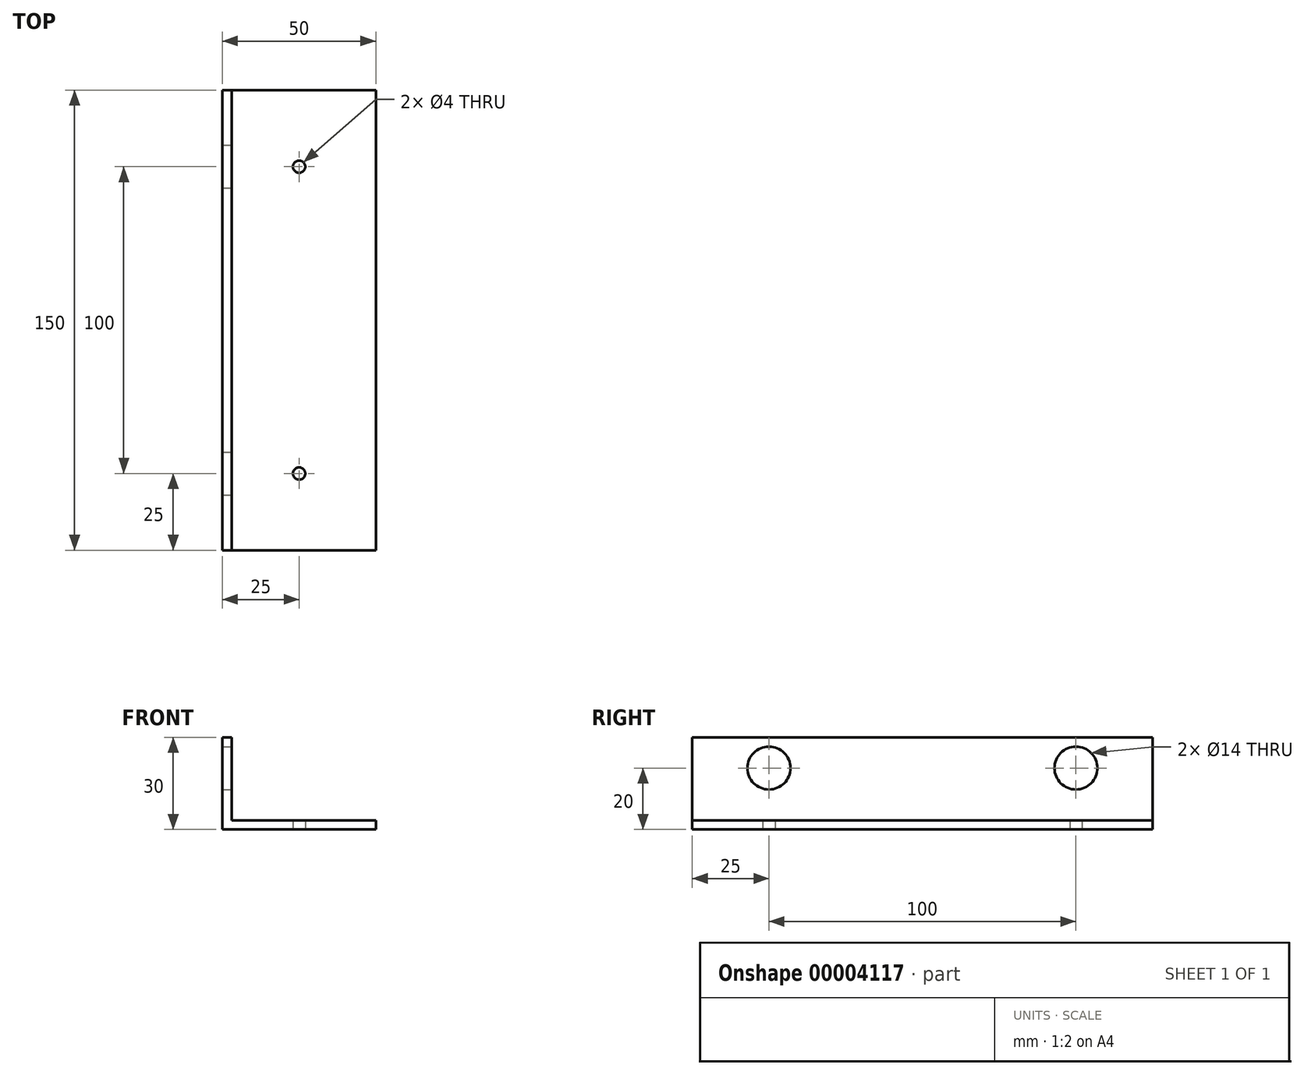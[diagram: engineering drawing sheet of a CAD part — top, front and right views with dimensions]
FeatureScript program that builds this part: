
annotation { "Feature Type Name" : "Feature", "Feature Type Description" : "" }
export const myFeature = defineFeature(function(context is Context, id is Id, definition is map)
    precondition{}
    {
        {
            var Q0;
            Q0=qCreatedBy(makeId("Front.planeOp"),FACE);
            var sketch = newSketch(context, id + "F0", { "sketchPlane" : qUnion([Q0])});
            skLineSegment(sketch, "E0", {"start": v(0, 0) * mm, "end": v(0, 30) * mm});
            skLineSegment(sketch, "E1", {"start": v(0, 30) * mm, "end": v(3, 30) * mm});
            skLineSegment(sketch, "E2", {"start": v(3, 30) * mm, "end": v(3, 3) * mm});
            skLineSegment(sketch, "E3", {"start": v(3, 3) * mm, "end": v(50, 3) * mm});
            skLineSegment(sketch, "E4", {"start": v(50, 3) * mm, "end": v(50, 0) * mm});
            skLineSegment(sketch, "E5", {"start": v(50, 0) * mm, "end": v(0, 0) * mm});
            skSolve(sketch);
        }
        {
            var Q0;
            Q0=makeQuery(id+"F0.imprint","IMPRINT",FACE,{"disambiguationData":[TD([[makeQuery(id+"F0.imprint","IMPRINT",EDGE,{"derivedFrom":sQuery(id+"F0.wireOp",EDGE,"E0")}),-1.0]])]});
            extrude(context, id + "F1", {"entities" : qUnion([Q0]), "depth" : 150 * mm});
        }
        {
            var Q0;
            Q0=makeQuery(id+"F1.opExtrude","SWEPT_FACE",FACE,{"disambiguationData":[OSD([sQuery(id+"F0.wireOp",EDGE,"E2")])]});
            var sketch = newSketch(context, id + "F2", { "sketchPlane" : qUnion([Q0])});
            skLineSegment(sketch, "E6", {"start": v(-150, 20) * mm, "end": v(0, 20) * mm});
            skCircle(sketch, "E7", {"center": v(-125, 20) * mm, "radius": 7 * mm});
            skCircle(sketch, "E8", {"center": v(-25, 20) * mm, "radius": 7 * mm});
            skSolve(sketch);
        }
        {
            var Q0;
            Q0=makeQuery(id+"F1.opExtrude","SWEPT_FACE",FACE,{"disambiguationData":[OSD([sQuery(id+"F0.wireOp",EDGE,"E5")])]});
            var sketch = newSketch(context, id + "F3", { "sketchPlane" : qUnion([Q0])});
            skLineSegment(sketch, "E9", {"start": v(25, 150) * mm, "end": v(25, 0) * mm});
            skCircle(sketch, "E10", {"center": v(25, 25) * mm, "radius": 2 * mm});
            skCircle(sketch, "E11", {"center": v(25, 125) * mm, "radius": 2 * mm});
            skSolve(sketch);
        }
        {
            var Q0;
            {var subQ0=sQuery(id+"F3.wireOp",EDGE,"E11");var subQ1=sQuery(id+"F3.wireOp",EDGE,"E9");var subQ3=makeQuery(id+"F3.imprint","INTERSECT",VERTEX,{"disambiguationData":[OD(0.0)],"derivedFrom":[subQ1,subQ0]});Q0=makeQuery(id+"F3.imprint","IMPRINT",FACE,{"disambiguationData":[TD([[makeQuery(id+"F3.imprint","IMPRINT",EDGE,{"disambiguationData":[TD([[subQ3,-1.0]])],"derivedFrom":subQ1}),1.0]])]});}
            var Q1;
            {var subQ0=sQuery(id+"F3.wireOp",EDGE,"E11");var subQ1=sQuery(id+"F3.wireOp",EDGE,"E9");var subQ3=makeQuery(id+"F3.imprint","INTERSECT",VERTEX,{"disambiguationData":[OD(0.0)],"derivedFrom":[subQ1,subQ0]});Q1=makeQuery(id+"F3.imprint","IMPRINT",FACE,{"disambiguationData":[TD([[makeQuery(id+"F3.imprint","IMPRINT",EDGE,{"disambiguationData":[TD([[subQ3,-1.0]])],"derivedFrom":subQ1}),-1.0]])]});}
            var Q2;
            {var subQ0=sQuery(id+"F3.wireOp",EDGE,"E10");var subQ1=sQuery(id+"F3.wireOp",EDGE,"E9");var subQ3=makeQuery(id+"F3.imprint","INTERSECT",VERTEX,{"disambiguationData":[OD(0.0)],"derivedFrom":[subQ1,subQ0]});Q2=makeQuery(id+"F3.imprint","IMPRINT",FACE,{"disambiguationData":[TD([[makeQuery(id+"F3.imprint","IMPRINT",EDGE,{"disambiguationData":[TD([[subQ3,-1.0]])],"derivedFrom":subQ1}),-1.0]])]});}
            var Q3;
            {var subQ0=sQuery(id+"F3.wireOp",EDGE,"E10");var subQ1=sQuery(id+"F3.wireOp",EDGE,"E9");var subQ3=makeQuery(id+"F3.imprint","INTERSECT",VERTEX,{"disambiguationData":[OD(0.0)],"derivedFrom":[subQ1,subQ0]});Q3=makeQuery(id+"F3.imprint","IMPRINT",FACE,{"disambiguationData":[TD([[makeQuery(id+"F3.imprint","IMPRINT",EDGE,{"disambiguationData":[TD([[subQ3,-1.0]])],"derivedFrom":subQ1}),1.0]])]});}
            extrude(context, id + "F4", {"entities" : qUnion([Q0, Q1, Q2, Q3]), "operationType" : NewBodyOperationType.REMOVE, "oppositeDirection" : true, "depth" : 25 * mm});
        }
        {
            var Q0;
            {var subQ0=sQuery(id+"F2.wireOp",EDGE,"E7");var subQ1=sQuery(id+"F2.wireOp",EDGE,"E6");var subQ3=makeQuery(id+"F2.imprint","INTERSECT",VERTEX,{"disambiguationData":[OD(0.0)],"derivedFrom":[subQ1,subQ0]});Q0=makeQuery(id+"F2.imprint","IMPRINT",FACE,{"disambiguationData":[TD([[makeQuery(id+"F2.imprint","IMPRINT",EDGE,{"disambiguationData":[TD([[subQ3,-1.0]])],"derivedFrom":subQ1}),-1.0]])]});}
            var Q1;
            {var subQ0=sQuery(id+"F2.wireOp",EDGE,"E7");var subQ1=sQuery(id+"F2.wireOp",EDGE,"E6");var subQ3=makeQuery(id+"F2.imprint","INTERSECT",VERTEX,{"disambiguationData":[OD(0.0)],"derivedFrom":[subQ1,subQ0]});Q1=makeQuery(id+"F2.imprint","IMPRINT",FACE,{"disambiguationData":[TD([[makeQuery(id+"F2.imprint","IMPRINT",EDGE,{"disambiguationData":[TD([[subQ3,-1.0]])],"derivedFrom":subQ1}),1.0]])]});}
            var Q2;
            {var subQ0=sQuery(id+"F2.wireOp",EDGE,"E8");var subQ1=sQuery(id+"F2.wireOp",EDGE,"E6");var subQ3=makeQuery(id+"F2.imprint","INTERSECT",VERTEX,{"disambiguationData":[OD(0.0)],"derivedFrom":[subQ1,subQ0]});Q2=makeQuery(id+"F2.imprint","IMPRINT",FACE,{"disambiguationData":[TD([[makeQuery(id+"F2.imprint","IMPRINT",EDGE,{"disambiguationData":[TD([[subQ3,-1.0]])],"derivedFrom":subQ1}),-1.0]])]});}
            var Q3;
            {var subQ0=sQuery(id+"F2.wireOp",EDGE,"E8");var subQ1=sQuery(id+"F2.wireOp",EDGE,"E6");var subQ3=makeQuery(id+"F2.imprint","INTERSECT",VERTEX,{"disambiguationData":[OD(0.0)],"derivedFrom":[subQ1,subQ0]});Q3=makeQuery(id+"F2.imprint","IMPRINT",FACE,{"disambiguationData":[TD([[makeQuery(id+"F2.imprint","IMPRINT",EDGE,{"disambiguationData":[TD([[subQ3,-1.0]])],"derivedFrom":subQ1}),1.0]])]});}
            extrude(context, id + "F5", {"entities" : qUnion([Q0, Q1, Q2, Q3]), "operationType" : NewBodyOperationType.REMOVE, "oppositeDirection" : true, "depth" : 25 * mm});
        }
    });
